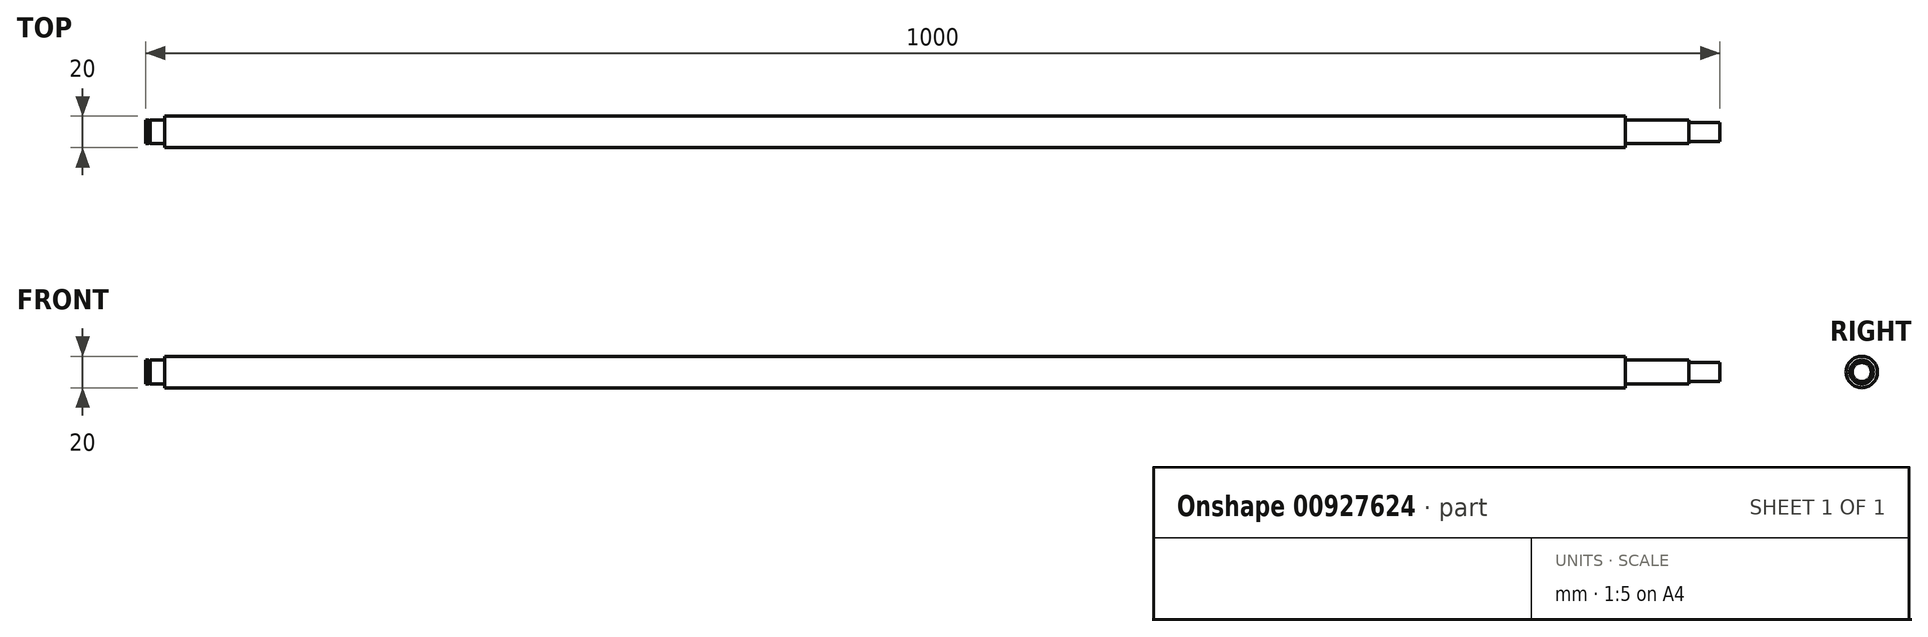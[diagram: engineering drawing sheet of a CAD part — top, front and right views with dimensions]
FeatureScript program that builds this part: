
annotation { "Feature Type Name" : "Feature", "Feature Type Description" : "" }
export const myFeature = defineFeature(function(context is Context, id is Id, definition is map)
    precondition{}
    {
        {
            var Q0;
            Q0=qCreatedBy(makeId("Right.planeOp"),FACE);
            var sketch = newSketch(context, id + "F0", { "sketchPlane" : qUnion([Q0])});
            skCircle(sketch, "E0", {"center": v(0, 0) * mm, "radius": 10 * mm});
            skSolve(sketch);
        }
        {
            var Q0;
            Q0=makeQuery(id+"F0.imprint","IMPRINT",FACE,{"disambiguationData":[TD([[makeQuery(id+"F0.imprint","IMPRINT",EDGE,{"derivedFrom":sQuery(id+"F0.wireOp",EDGE,"E0")}),1.0]])]});
            extrude(context, id + "F1", {"entities" : qUnion([Q0]), "oppositeDirection" : true, "depth" : 1000 * mm, "offsetDistance" : 25 * mm});
        }
        {
            var Q0;
            Q0=makeQuery(id+"F1.opExtrude","CAP_FACE",FACE,{"disambiguationData":[OSD([sQuery(id+"F0.wireOp",EDGE,"E0")])],"isStart":true});
            var sketch = newSketch(context, id + "F2", { "sketchPlane" : qUnion([Q0])});
            skCircle(sketch, "E1", {"center": v(0, 0) * mm, "radius": 6 * mm});
            skSolve(sketch);
        }
        {
            var Q0;
            Q0=makeQuery(id+"F2.imprint","IMPRINT",FACE,{"disambiguationData":[TD([[makeQuery(id+"F2.imprint","IMPRINT",EDGE,{"derivedFrom":sQuery(id+"F2.wireOp",EDGE,"E1")}),-1.0]])]});
            extrude(context, id + "F3", {"entities" : qUnion([Q0]), "operationType" : NewBodyOperationType.REMOVE, "oppositeDirection" : true, "depth" : 20 * mm, "offsetDistance" : 25 * mm});
        }
        {
            var Q0;
            Q0=makeQuery(id+"F3.boolean.opBoolean","COPY",FACE,{"derivedFrom":makeQuery(id+"F3.opExtrude","CAP_FACE",FACE,{"disambiguationData":[OSD([sQuery(id+"F0.wireOp",EDGE,"E0"),sQuery(id+"F2.wireOp",EDGE,"E1")])],"isStart":false})});
            var sketch = newSketch(context, id + "F4", { "sketchPlane" : qUnion([Q0])});
            skCircle(sketch, "E2", {"center": v(0, 0) * mm, "radius": 7.5 * mm});
            skSolve(sketch);
        }
        {
            var Q0;
            Q0=makeQuery(id+"F4.imprint","IMPRINT",FACE,{"disambiguationData":[TD([[makeQuery(id+"F4.imprint","IMPRINT",EDGE,{"derivedFrom":sQuery(id+"F4.wireOp",EDGE,"E2")}),-1.0]])]});
            extrude(context, id + "F5", {"entities" : qUnion([Q0]), "operationType" : NewBodyOperationType.REMOVE, "oppositeDirection" : true, "depth" : 40 * mm, "offsetDistance" : 25 * mm});
        }
        {
            var Q0;
            Q0=makeQuery(id+"F1.opExtrude","CAP_FACE",FACE,{"disambiguationData":[OSD([sQuery(id+"F0.wireOp",EDGE,"E0")])],"isStart":false});
            var sketch = newSketch(context, id + "F6", { "sketchPlane" : qUnion([Q0])});
            skCircle(sketch, "E3", {"center": v(0, 0) * mm, "radius": 7.5 * mm});
            skSolve(sketch);
        }
        {
            var Q0;
            Q0=makeQuery(id+"F6.imprint","IMPRINT",FACE,{"disambiguationData":[TD([[makeQuery(id+"F6.imprint","IMPRINT",EDGE,{"derivedFrom":sQuery(id+"F6.wireOp",EDGE,"E3")}),-1.0]])]});
            extrude(context, id + "F7", {"entities" : qUnion([Q0]), "operationType" : NewBodyOperationType.REMOVE, "oppositeDirection" : true, "depth" : 12 * mm, "offsetDistance" : 25 * mm});
        }
        {
            var Q0;
            Q0=qCreatedBy(makeId("Front.planeOp"),FACE);
            var sketch = newSketch(context, id + "F8", { "sketchPlane" : qUnion([Q0])});
            skLineSegment(sketch, "E4", {"start": v(-988, 91.83) * mm, "end": v(-988, -84.53) * mm, "construction": true});
            skLineSegment(sketch, "E5", {"start": v(-998.15, 29.52) * mm, "end": v(-998.15, -20.6) * mm, "construction": true});
            skLineSegment(sketch, "E6", {"start": v(-1003.55, 0) * mm, "end": v(-969.72, 0) * mm, "construction": true});
            skLineSegment(sketch, "E7", {"start": v(-1002.51, 7.5) * mm, "end": v(-978.27, 7.5) * mm, "construction": true});
            skPoint(sketch, "E8", {"position": v(-998.15, 7.5) * mm});
            skLineSegment(sketch, "E9", {"start": v(-998.15, 7.5) * mm, "end": v(-998.15, 7.15) * mm});
            skLineSegment(sketch, "E10", {"start": v(-998.15, 7.15) * mm, "end": v(-997, 7.15) * mm});
            skLineSegment(sketch, "E11", {"start": v(-997, 7.15) * mm, "end": v(-997, 7.5) * mm});
            skLineSegment(sketch, "E12", {"start": v(-997, 7.5) * mm, "end": v(-998.15, 7.5) * mm});
            skSolve(sketch);
        }
        {
            var Q0;
            Q0 = qSketchRegion(id + "F8", true);
            var Q1;
            Q1=sQuery(id+"F8.wireOp",EDGE,"E6");
            revolve(context, id + "F9", {"operationType" : NewBodyOperationType.REMOVE, "surfaceOperationType" : NewSurfaceOperationType.NEW, "entities" : qUnion([Q0]), "axis" : qUnion([Q1]), "revolveType" : RevolveType.FULL, "oppositeDirection" : true});
        }
    });
